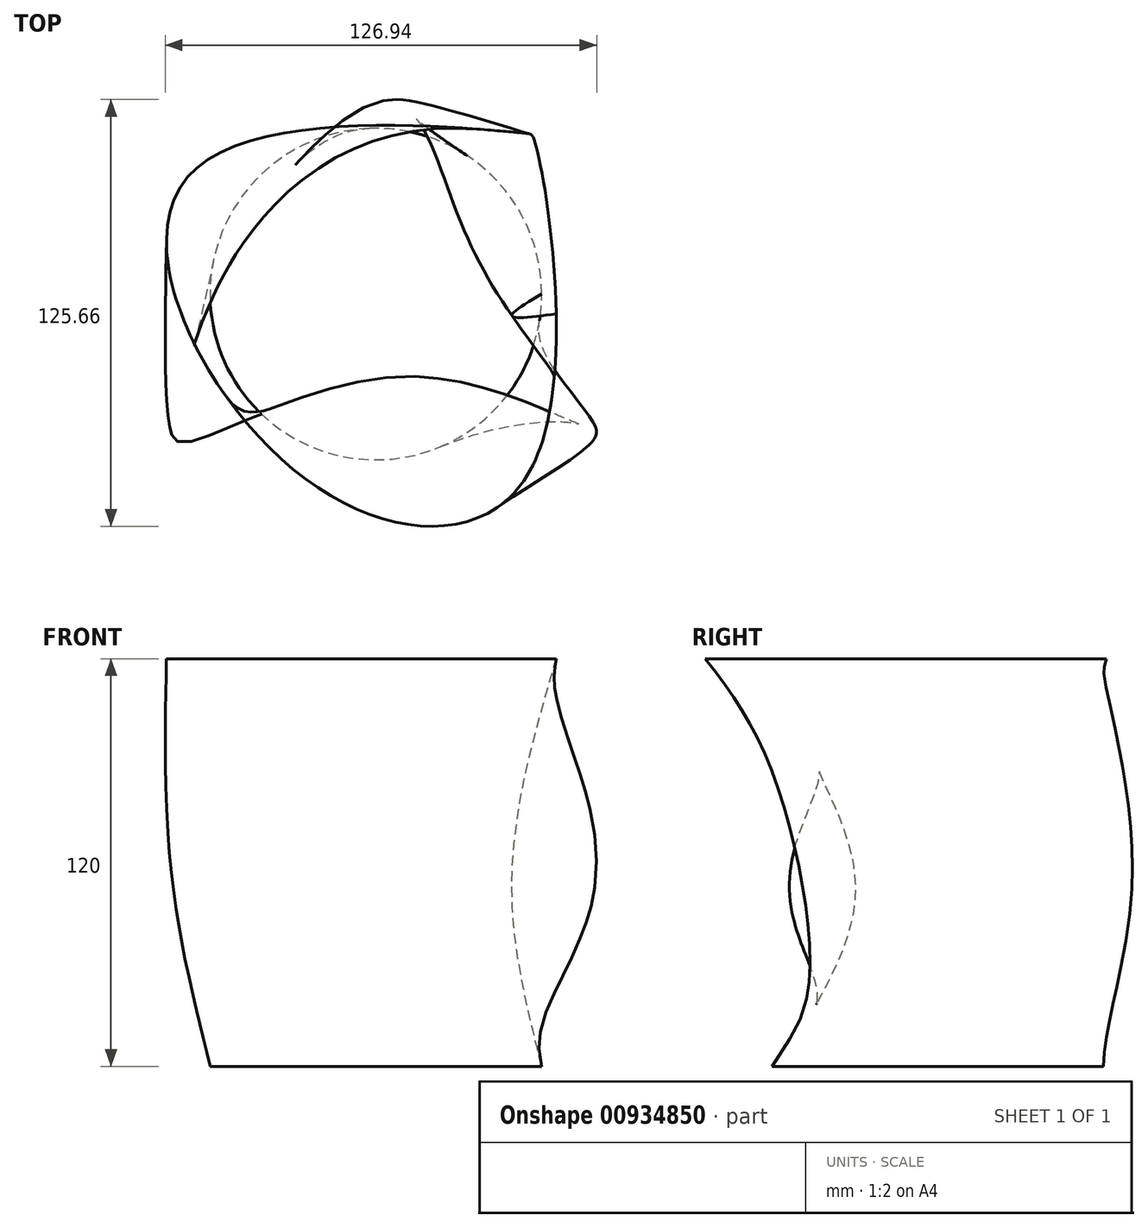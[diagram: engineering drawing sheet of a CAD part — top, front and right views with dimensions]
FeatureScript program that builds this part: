
annotation { "Feature Type Name" : "Feature", "Feature Type Description" : "" }
export const myFeature = defineFeature(function(context is Context, id is Id, definition is map)
    precondition{}
    {
        {
            var Q0;
            Q0=qCreatedBy(makeId("Top.planeOp"),FACE);
            var sketch = newSketch(context, id + "F0", { "sketchPlane" : qUnion([Q0])});
            skCircle(sketch, "E0", {"center": v(0, 0) * mm, "radius": 48.8 * mm});
            skSolve(sketch);
        }
        {
            var Q0;
            Q0=qCreatedBy(makeId("Top.planeOp"),FACE);
            cPlane(context, id + "F1", {"entities" : qUnion([Q0]), "cplaneType" : CPlaneType.OFFSET, "offset" : 50 * mm, "width" : 150 * mm, "height" : 150 * mm});
        }
        {
            var Q0;
            Q0=qCreatedBy(id+"F1.planeOp",FACE);
            var sketch = newSketch(context, id + "F2", { "sketchPlane" : qUnion([Q0])});
            skFitSpline(sketch, "E1", {"points": [v(-39.81, 14.72) * mm, v(5.56, 56.79) * mm, v(31.1, 8.41) * mm, v(63.85, -39.06) * mm, v(11.27, -24.34) * mm, v(-56.34, -43.57) * mm, v(-59.34, -39.36) * mm, v(-39.81, 14.72) * mm]});
            skSolve(sketch);
        }
        {
            var Q0;
            Q0=qCreatedBy(id+"F1.planeOp",FACE);
            cPlane(context, id + "F3", {"entities" : qUnion([Q0]), "cplaneType" : CPlaneType.OFFSET, "offset" : 70 * mm, "width" : 150 * mm, "height" : 150 * mm});
        }
        {
            var Q0;
            Q0=qCreatedBy(id+"F3.planeOp",FACE);
            var sketch = newSketch(context, id + "F4", { "sketchPlane" : qUnion([Q0])});
            skFitSpline(sketch, "E2", {"points": [v(-54.23, 35.75) * mm, v(42.82, 47.47) * mm, v(46.72, 45.07) * mm, v(45.22, -52.28) * mm, v(-21.18, -54.08) * mm, v(-54.23, 35.75) * mm]});
            skSolve(sketch);
        }
        {
            var Q0;
            Q0=makeQuery(id+"F0.imprint","IMPRINT",FACE,{"disambiguationData":[TD([[makeQuery(id+"F0.imprint","IMPRINT",EDGE,{"derivedFrom":sQuery(id+"F0.wireOp",EDGE,"E0")}),1.0]])]});
            var Q1;
            Q1=makeQuery(id+"F2.imprint","IMPRINT",FACE,{"disambiguationData":[TD([[makeQuery(id+"F2.imprint","IMPRINT",EDGE,{"derivedFrom":sQuery(id+"F2.wireOp",EDGE,"E1")}),-1.0]])]});
            var Q2;
            Q2=makeQuery(id+"F4.imprint","IMPRINT",FACE,{"disambiguationData":[TD([[makeQuery(id+"F4.imprint","IMPRINT",EDGE,{"derivedFrom":sQuery(id+"F4.wireOp",EDGE,"E2")}),-1.0]])]});
            var Q3;
            Q3=sQuery(id+"F0.wireOp",EDGE,"E0");
            var Q4;
            Q4=makeQuery(id+"F2.imprint","IMPRINT",FACE,{"disambiguationData":[TD([[makeQuery(id+"F2.imprint","IMPRINT",EDGE,{"derivedFrom":sQuery(id+"F2.wireOp",EDGE,"E1")}),-1.0]])]});
            var Q5;
            Q5=makeQuery(id+"F4.imprint","IMPRINT",FACE,{"disambiguationData":[TD([[makeQuery(id+"F4.imprint","IMPRINT",EDGE,{"derivedFrom":sQuery(id+"F4.wireOp",EDGE,"E2")}),-1.0]])]});
            loft(context, id + "F5", {"bodyType" : ToolBodyType.SURFACE, "sheetProfilesArray" : [{ "sheetProfileEntities" : qUnion([Q0]) }, { "sheetProfileEntities" : qUnion([Q1]) }, { "sheetProfileEntities" : qUnion([Q2]) }], "wireProfilesArray" : [{ "wireProfileEntities" : qUnion([Q3]) }, { "wireProfileEntities" : qUnion([Q4]) }, { "wireProfileEntities" : qUnion([Q5]) }]});
        }
    });
